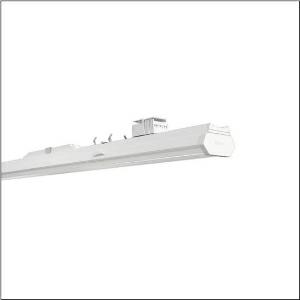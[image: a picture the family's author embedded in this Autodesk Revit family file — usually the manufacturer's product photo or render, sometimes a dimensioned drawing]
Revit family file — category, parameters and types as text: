
# Revit family: licross_11_protected_ho_51tp12dn4fxm3s4
name_source: partatom
category: Lighting Fixtures
units: mm (PartAtom-declared; Revit-internal decimal feet)

## family parameters
Cut with Voids When Loaded = No
Host = Face
Light Source = No
Part Type = Normal
Room Calculation Point = No
Round Connector Dimension = Use Diameter
Shared = No

## types (1)
- --- (1 x LED, 970 lm, 7.4 W, 4000K)
    Apparent Load = 7 VA
    CIE Flux Codes = 70 91 97 98 100
    Color Rendering = 80
    Color Temperature = 4000K
    Default Elevation = 1800 mm
    Description = Licross 11 Protected HO, luminaire insert, of sheet steel, galvanised, coil coated, white, length: 1.500mm, width: 90mm, height: 101mm, LED rated luminous flux: 15.270lm, light colour: 840, SDCM (Standard Deviation of Colour Matching)MacAdam ≤ 2 SDCM (initial), control gear: DALI 2, with plug, 6-pole, with phase selection, for trunking rail, 9 or 11-core, mains connection: 220..240V, AC, 50/60Hz, rated input power: 91W, for trunking rail, 9-/11-core, internal wiring halogen-free, for emergency light function, converter,control gear: single battery element, battery: LiFePO4, 9Ah, primary light control with lens, of plastic, primary optical cover: cover, of PMMA, light emission: direct distribution, primary light characteristic: symmetric, protection rating (complete): IP64, insulation class (complete): insulation class I (protective earthing), certification: CE, UKCA, protection symbol: D if used in an environment with conductive dust loads with corresponding accessories, impact resistance: IK06, permissible ambient temperature for indoor applications: +5..+30°C, standard: EN 60598-2-22, LABS conformity tested according to VDMA 24364:2018-05, reducing of maximum allowable ambient temperature of 5°C with ceiling mounting, corresponds to IFS (International Featured Standards) requirements for safety and quality in the food industry, The light source and the operating device comply with the requirements of the Ecodesign Regulation (EU) 2019/2020 and are replaceable in accordance with this regulation, packaging unit: 1 piece
    Height = 92 mm
    Lamp = 1 x LED
    Lamp Light Flux = 970 lm
    Lamp Power = 7.4 W
    Lamp count = 1
    Length = 1500 mm
    Luminous efficacy = 131 lm/W
    Manufacturer = Siteco
    ModVariant = No
    Model = 51TP12DN4FXM3S4
    Mounting Place = Ceiling
    Mounting Type = Pendant
    Number of Poles = 1
    OnlyDefault = Yes
    Power Factor = 1
    Product Name = Licross 11 Protected HO
    Product group = luminaire insert | ceiling pendant
    ProductGroupID = 901
    Protection Class = Protection class I
    Protection Degree = IP 64
    RLX_Detail_Level = 1
    RLX_Emergency_Light_Flux = 0 lm
    RLX_Emergency_Type = 0
    RLX_Emergency_Type_DB = No
    RlxData = <blob elided: 25157 chars, md5=5bece6a1>
    Socket = socket
    Standby Power = 0 W
    System Light Flux = 970 lm
    System Power = 7 W
    Type Comments = : emergency light operation: 3 h
    Type Image = l_1256148.jpg
    URL = http://relux.com
    VarID = @adj_094699
    Voltage = 0 V
    Weight = 0.00 kg
    Width = 88 mm

## geometry (parser evidence)
native form markers: Blend x4, Sweep x10
no freeform markers — native parametric forms only
